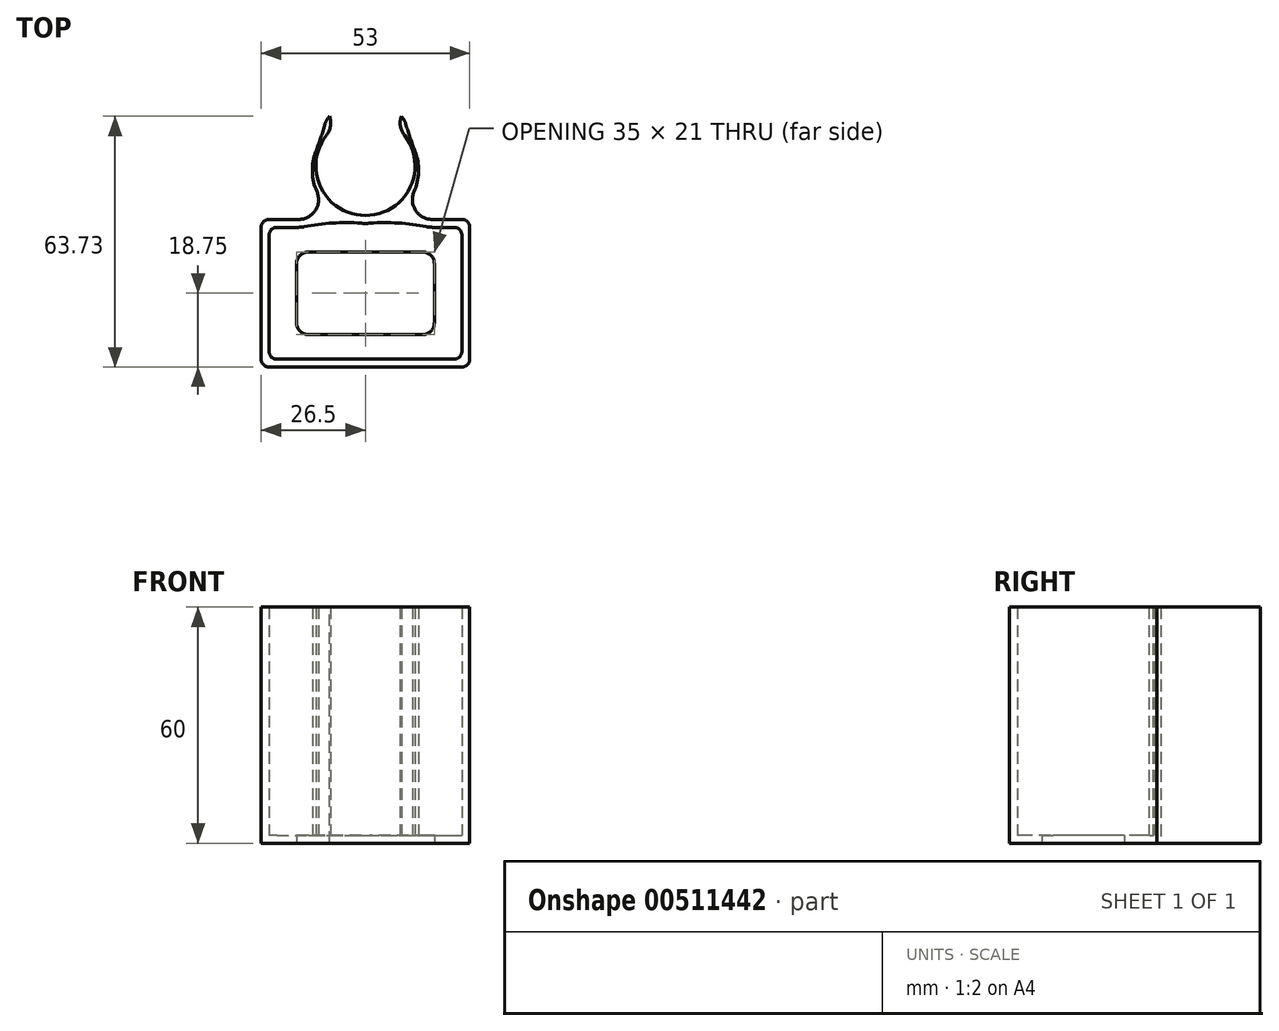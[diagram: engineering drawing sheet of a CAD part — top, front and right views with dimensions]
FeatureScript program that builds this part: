
annotation { "Feature Type Name" : "Feature", "Feature Type Description" : "" }
export const myFeature = defineFeature(function(context is Context, id is Id, definition is map)
    precondition{}
    {
        {
            assignVariable(context, id + "F0", {"variableType" : VariableType.LENGTH, "name" : "RodDiam", "lengthValue" : 25.2 * mm});
        }
        {
            assignVariable(context, id + "F1", {"variableType" : VariableType.LENGTH, "name" : "BaseThickness", "lengthValue" : 2 * mm});
        }
        {
            assignVariable(context, id + "F2", {"variableType" : VariableType.LENGTH, "name" : "BaseWidth", "lengthValue" : 53 * mm});
        }
        {
            assignVariable(context, id + "F3", {"variableType" : VariableType.LENGTH, "name" : "PocketHeight", "lengthValue" : 60 * mm});
        }
        {
            var Q0;
            Q0=qCreatedBy(makeId("Top.planeOp"),FACE);
            var sketch = newSketch(context, id + "F4", { "sketchPlane" : qUnion([Q0])});
            skLineSegment(sketch, "E0", {"start": v(0, 0) * mm, "end": v(0, 1) * mm, "construction": true});
            skLineSegment(sketch, "E1", {"start": v(0, 0) * mm, "end": v(0, -1) * mm, "construction": true});
            skLineSegment(sketch, "E2.bottom", {"start": v(-26.5, -2) * mm, "end": v(26.5, -2) * mm});
            skLineSegment(sketch, "E2.top", {"start": v(-26.5, 0) * mm, "end": v(26.5, 0) * mm});
            skLineSegment(sketch, "E2.left", {"start": v(-26.5, -2) * mm, "end": v(-26.5, 0) * mm});
            skLineSegment(sketch, "E2.right", {"start": v(26.5, -2) * mm, "end": v(26.5, 0) * mm});
            skPoint(sketch, "E2.middle", {"position": v(0, -1) * mm});
            skLineSegment(sketch, "E3", {"start": v(0, 1) * mm, "end": v(0, 13.6) * mm, "construction": true});
            skLineSegment(sketch, "E4", {"start": v(0, 13.6) * mm, "end": v(8.05, 23.29) * mm, "construction": true});
            skLineSegment(sketch, "E5", {"start": v(0, 1) * mm, "end": v(8.05, 23.29) * mm, "construction": true});
            skLineSegment(sketch, "E6.MirrorCS", {"start": v(0, 13.6) * mm, "end": v(-8.05, 23.29) * mm, "construction": true});
            skArc(sketch, "E7", {"start": v(-8.05, 23.29) * mm, "mid": v(0, 1) * mm, "end": v(8.05, 23.29) * mm});
            skArc(sketch, "E8", {"start": v(-8.05, 23.29) * mm, "mid": v(0, -1) * mm, "end": v(8.05, 23.29) * mm});
            skLineSegment(sketch, "E9", {"start": v(8.05, 23.29) * mm, "end": v(9.41, 27.05) * mm});
            skLineSegment(sketch, "E10", {"start": v(9.41, 27.05) * mm, "end": v(9.41, 22.13) * mm});
            skLineSegment(sketch, "E11.MirrorCS", {"start": v(-8.05, 23.29) * mm, "end": v(-9.41, 27.05) * mm});
            skLineSegment(sketch, "E12.MirrorCS", {"start": v(-9.41, 27.05) * mm, "end": v(-9.41, 22.13) * mm});
            skLineSegment(sketch, "E13.top", {"start": v(-26.5, -37.5) * mm, "end": v(26.5, -37.5) * mm});
            skLineSegment(sketch, "E13.left", {"start": v(-26.5, -2) * mm, "end": v(-26.5, -37.5) * mm});
            skLineSegment(sketch, "E13.right", {"start": v(26.5, -2) * mm, "end": v(26.5, -37.5) * mm});
            skSolve(sketch);
        }
        {
            var Q0;
            Q0=qSketchRegion(id+"F4",true);
            extrude(context, id + "F5", {"entities" : qUnion([Q0]), "depth" : getVariable(context, 'PocketHeight'), "offsetDistance" : 25 * mm});
        }
        {
            var Q0;
            Q0=makeQuery(id+"F5.opExtrude","SWEPT_EDGE",EDGE,{"disambiguationData":[OSD([sQuery(id+"F4.wireOp",EDGE,"E8"),sQuery(id+"F4.wireOp",EDGE,"E12.MirrorCS")])]});
            var Q1;
            Q1=makeQuery(id+"F5.opExtrude","SWEPT_EDGE",EDGE,{"disambiguationData":[OSD([sQuery(id+"F4.wireOp",EDGE,"E8"),sQuery(id+"F4.wireOp",EDGE,"E10")])]});
            fillet(context, id + "F6", {"entities" : qUnion([Q0, Q1]), "radius" : getVariable(context, 'RodDiam') * 5, "tangentPropagation" : true, "allowEdgeOverflow" : false});
        }
        {
            var Q0;
            {var subQ0=sQuery(id+"F4.wireOp",EDGE,"E8");var subQ1=sQuery(id+"F4.wireOp",EDGE,"E2.top");Q0=makeQuery(id+"F5.opExtrude","SWEPT_EDGE",EDGE,{"disambiguationData":[OSD([subQ1,subQ0]),TDD([makeQuery(id+"F4.imprint","INTERSECT",VERTEX,{"disambiguationData":[OD(0.0)],"derivedFrom":[subQ1,subQ0]})])]});}
            var Q1;
            {var subQ0=sQuery(id+"F4.wireOp",EDGE,"E8");var subQ1=sQuery(id+"F4.wireOp",EDGE,"E2.top");Q1=makeQuery(id+"F5.opExtrude","SWEPT_EDGE",EDGE,{"disambiguationData":[OSD([subQ1,subQ0]),TDD([makeQuery(id+"F4.imprint","INTERSECT",VERTEX,{"disambiguationData":[OD(1.0)],"derivedFrom":[subQ1,subQ0]})])]});}
            fillet(context, id + "F7", {"entities" : qUnion([Q0, Q1]), "radius" : getVariable(context, 'RodDiam') / 5, "tangentPropagation" : true, "allowEdgeOverflow" : false});
        }
        {
            var Q0;
            Q0=makeQuery(id+"F5.opExtrude","SWEPT_EDGE",EDGE,{"disambiguationData":[OSD([sQuery(id+"F4.wireOp",EDGE,"E7"),sQuery(id+"F4.wireOp",EDGE,"E8"),sQuery(id+"F4.wireOp",EDGE,"E9")])]});
            var Q1;
            Q1=makeQuery(id+"F5.opExtrude","SWEPT_EDGE",EDGE,{"disambiguationData":[OSD([sQuery(id+"F4.wireOp",EDGE,"E7"),sQuery(id+"F4.wireOp",EDGE,"E8"),sQuery(id+"F4.wireOp",EDGE,"E11.MirrorCS")])]});
            fillet(context, id + "F8", {"entities" : qUnion([Q0, Q1]), "radius" : getVariable(context, 'RodDiam') / 5, "tangentPropagation" : true, "allowEdgeOverflow" : false});
        }
        {
            var Q0;
            Q0=makeQuery(id+"F6.opFillet","BLEND_EDGE",EDGE,{"blendedFrom":[makeQuery(id+"F5.opExtrude","SWEPT_EDGE",EDGE,{"disambiguationData":[OSD([sQuery(id+"F4.wireOp",EDGE,"E8"),sQuery(id+"F4.wireOp",EDGE,"E10")])]}),makeQuery(id+"F5.opExtrude","SWEPT_FACE",FACE,{"disambiguationData":[OSD([sQuery(id+"F4.wireOp",EDGE,"E9")])]})],"blendedInto":[makeQuery(id+"F5.opExtrude","SWEPT_FACE",FACE,{"disambiguationData":[OSD([sQuery(id+"F4.wireOp",EDGE,"E9")])]})]});
            var Q1;
            Q1=makeQuery(id+"F6.opFillet","BLEND_EDGE",EDGE,{"blendedFrom":[makeQuery(id+"F5.opExtrude","SWEPT_EDGE",EDGE,{"disambiguationData":[OSD([sQuery(id+"F4.wireOp",EDGE,"E8"),sQuery(id+"F4.wireOp",EDGE,"E12.MirrorCS")])]}),makeQuery(id+"F5.opExtrude","SWEPT_FACE",FACE,{"disambiguationData":[OSD([sQuery(id+"F4.wireOp",EDGE,"E11.MirrorCS")])]})],"blendedInto":[makeQuery(id+"F5.opExtrude","SWEPT_FACE",FACE,{"disambiguationData":[OSD([sQuery(id+"F4.wireOp",EDGE,"E11.MirrorCS")])]})]});
            fillet(context, id + "F9", {"entities" : qUnion([Q0, Q1]), "radius" : getVariable(context, 'RodDiam') / 5, "tangentPropagation" : true, "allowEdgeOverflow" : false});
        }
        {
            var Q0;
            Q0=makeQuery(id+"F5.opExtrude","CAP_FACE",FACE,{"disambiguationData":[OSD([sQuery(id+"F4.wireOp",EDGE,"E2.top"),sQuery(id+"F4.wireOp",EDGE,"E2.left"),sQuery(id+"F4.wireOp",EDGE,"E2.right"),sQuery(id+"F4.wireOp",EDGE,"E7"),sQuery(id+"F4.wireOp",EDGE,"E8"),sQuery(id+"F4.wireOp",EDGE,"E9"),sQuery(id+"F4.wireOp",EDGE,"E10"),sQuery(id+"F4.wireOp",EDGE,"E11.MirrorCS"),sQuery(id+"F4.wireOp",EDGE,"E12.MirrorCS"),sQuery(id+"F4.wireOp",EDGE,"E13.top"),sQuery(id+"F4.wireOp",EDGE,"E13.left"),sQuery(id+"F4.wireOp",EDGE,"E13.right")])],"isStart":false});
            shell(context, id + "F10", {"entities" : qUnion([Q0]), "thickness" : 2 * mm});
        }
        {
            var Q0;
            Q0=makeQuery(id+"F5.opExtrude","CAP_FACE",FACE,{"disambiguationData":[OSD([sQuery(id+"F4.wireOp",EDGE,"E2.top"),sQuery(id+"F4.wireOp",EDGE,"E2.left"),sQuery(id+"F4.wireOp",EDGE,"E2.right"),sQuery(id+"F4.wireOp",EDGE,"E7"),sQuery(id+"F4.wireOp",EDGE,"E8"),sQuery(id+"F4.wireOp",EDGE,"E9"),sQuery(id+"F4.wireOp",EDGE,"E10"),sQuery(id+"F4.wireOp",EDGE,"E11.MirrorCS"),sQuery(id+"F4.wireOp",EDGE,"E12.MirrorCS"),sQuery(id+"F4.wireOp",EDGE,"E13.top"),sQuery(id+"F4.wireOp",EDGE,"E13.left"),sQuery(id+"F4.wireOp",EDGE,"E13.right")])],"isStart":true});
            var sketch = newSketch(context, id + "F11", { "sketchPlane" : qUnion([Q0])});
            skLineSegment(sketch, "E14", {"start": v(26.5, 18.75) * mm, "end": v(0, 18.75) * mm, "construction": true});
            skLineSegment(sketch, "E15.bottom", {"start": v(-17.5, 8.25) * mm, "end": v(17.5, 8.25) * mm});
            skLineSegment(sketch, "E15.top", {"start": v(-17.5, 29.25) * mm, "end": v(17.5, 29.25) * mm});
            skLineSegment(sketch, "E15.left", {"start": v(-17.5, 8.25) * mm, "end": v(-17.5, 29.25) * mm});
            skLineSegment(sketch, "E15.right", {"start": v(17.5, 8.25) * mm, "end": v(17.5, 29.25) * mm});
            skPoint(sketch, "E15.middle", {"position": v(0, 18.75) * mm});
            skSolve(sketch);
        }
        {
            var Q0;
            {var subQ0=sQuery(id+"F4.wireOp",EDGE,"E8");var subQ1=sQuery(id+"F4.wireOp",EDGE,"E2.top");Q0=makeQuery(id+"F10.opShell","TWEAK_EDGE",EDGE,{"derivedFrom":[makeQuery(id+"F7.opFillet","BLEND_FACE",FACE,{"disambiguationData":[OSD([subQ1,subQ0]),TDD([makeQuery(id+"F5.opExtrude","SWEPT_EDGE",EDGE,{"disambiguationData":[OSD([subQ1,subQ0]),TDD([makeQuery(id+"F4.imprint","INTERSECT",VERTEX,{"disambiguationData":[OD(1.0)],"derivedFrom":[subQ1,subQ0]})])]})])]}),makeQuery(id+"F5.opExtrude","SWEPT_FACE",FACE,{"disambiguationData":[OSD([sQuery(id+"F4.wireOp",EDGE,"E7")])]})]});}
            var Q1;
            {var subQ0=sQuery(id+"F4.wireOp",EDGE,"E8");var subQ1=sQuery(id+"F4.wireOp",EDGE,"E2.top");Q1=makeQuery(id+"F10.opShell","TWEAK_EDGE",EDGE,{"derivedFrom":[makeQuery(id+"F7.opFillet","BLEND_FACE",FACE,{"disambiguationData":[OSD([subQ1,subQ0]),TDD([makeQuery(id+"F5.opExtrude","SWEPT_EDGE",EDGE,{"disambiguationData":[OSD([subQ1,subQ0]),TDD([makeQuery(id+"F4.imprint","INTERSECT",VERTEX,{"disambiguationData":[OD(0.0)],"derivedFrom":[subQ1,subQ0]})])]})])]}),makeQuery(id+"F5.opExtrude","SWEPT_FACE",FACE,{"disambiguationData":[OSD([sQuery(id+"F4.wireOp",EDGE,"E7")])]})]});}
            fillet(context, id + "F12", {"entities" : qUnion([Q0, Q1]), "radius" : getVariable(context, 'BaseWidth'), "tangentPropagation" : true, "allowEdgeOverflow" : false});
        }
        {
            var Q0;
            Q0=makeQuery(id+"F5.opExtrude","SWEPT_EDGE",EDGE,{"disambiguationData":[OSD([sQuery(id+"F4.wireOp",EDGE,"E2.top"),sQuery(id+"F4.wireOp",EDGE,"E2.left")])]});
            var Q1;
            Q1=makeQuery(id+"F5.opExtrude","SWEPT_EDGE",EDGE,{"disambiguationData":[OSD([sQuery(id+"F4.wireOp",EDGE,"E2.top"),sQuery(id+"F4.wireOp",EDGE,"E2.right")])]});
            var Q2;
            Q2=makeQuery(id+"F10.opShell","OFFSET_EDGE",EDGE,{"disambiguationData":[OSD([sQuery(id+"F4.wireOp",EDGE,"E13.top"),sQuery(id+"F4.wireOp",EDGE,"E13.right")])]});
            var Q3;
            Q3=makeQuery(id+"F10.opShell","OFFSET_EDGE",EDGE,{"disambiguationData":[OSD([sQuery(id+"F4.wireOp",EDGE,"E13.top"),sQuery(id+"F4.wireOp",EDGE,"E13.left")])]});
            var Q4;
            Q4=makeQuery(id+"F5.opExtrude","SWEPT_EDGE",EDGE,{"disambiguationData":[OSD([sQuery(id+"F4.wireOp",EDGE,"E13.top"),sQuery(id+"F4.wireOp",EDGE,"E13.right")])]});
            var Q5;
            Q5=makeQuery(id+"F5.opExtrude","SWEPT_EDGE",EDGE,{"disambiguationData":[OSD([sQuery(id+"F4.wireOp",EDGE,"E13.top"),sQuery(id+"F4.wireOp",EDGE,"E13.left")])]});
            var Q6;
            Q6=makeQuery(id+"F10.opShell","OFFSET_EDGE",EDGE,{"disambiguationData":[OSD([sQuery(id+"F4.wireOp",EDGE,"E2.top"),sQuery(id+"F4.wireOp",EDGE,"E2.right")])]});
            var Q7;
            Q7=makeQuery(id+"F10.opShell","OFFSET_EDGE",EDGE,{"disambiguationData":[OSD([sQuery(id+"F4.wireOp",EDGE,"E2.top"),sQuery(id+"F4.wireOp",EDGE,"E2.left")])]});
            fillet(context, id + "F13", {"entities" : qUnion([Q0, Q1, Q2, Q3, Q4, Q5, Q6, Q7]), "radius" : getVariable(context, 'BaseThickness'), "tangentPropagation" : true, "allowEdgeOverflow" : false});
        }
        {
            var Q0;
            Q0=makeQuery(id+"F11.imprint","IMPRINT",FACE,{"disambiguationData":[TD([[makeQuery(id+"F11.imprint","IMPRINT",EDGE,{"derivedFrom":sQuery(id+"F11.wireOp",EDGE,"E15.bottom")}),1.0]])]});
            extrude(context, id + "F14", {"entities" : qUnion([Q0]), "operationType" : NewBodyOperationType.REMOVE, "oppositeDirection" : true, "depth" : 2 * mm, "offsetDistance" : 25 * mm});
        }
        {
            var Q0;
            Q0=makeQuery(id+"F14.boolean.opBoolean","COPY",EDGE,{"derivedFrom":makeQuery(id+"F14.opExtrude","SWEPT_EDGE",EDGE,{"disambiguationData":[OSD([sQuery(id+"F11.wireOp",EDGE,"E15.bottom"),sQuery(id+"F11.wireOp",EDGE,"E15.right")])]})});
            var Q1;
            Q1=makeQuery(id+"F14.boolean.opBoolean","COPY",EDGE,{"derivedFrom":makeQuery(id+"F14.opExtrude","SWEPT_EDGE",EDGE,{"disambiguationData":[OSD([sQuery(id+"F11.wireOp",EDGE,"E15.bottom"),sQuery(id+"F11.wireOp",EDGE,"E15.left")])]})});
            var Q2;
            Q2=makeQuery(id+"F14.boolean.opBoolean","COPY",EDGE,{"derivedFrom":makeQuery(id+"F14.opExtrude","SWEPT_EDGE",EDGE,{"disambiguationData":[OSD([sQuery(id+"F11.wireOp",EDGE,"E15.top"),sQuery(id+"F11.wireOp",EDGE,"E15.left")])]})});
            var Q3;
            Q3=makeQuery(id+"F14.boolean.opBoolean","COPY",EDGE,{"derivedFrom":makeQuery(id+"F14.opExtrude","SWEPT_EDGE",EDGE,{"disambiguationData":[OSD([sQuery(id+"F11.wireOp",EDGE,"E15.top"),sQuery(id+"F11.wireOp",EDGE,"E15.right")])]})});
            fillet(context, id + "F15", {"entities" : qUnion([Q0, Q1, Q2, Q3]), "tangentPropagation" : true, "radius" : 3 * mm, "defaultsChanged" : true, "vertexSettings" : [], "allowEdgeOverflow" : false});
        }
    });
